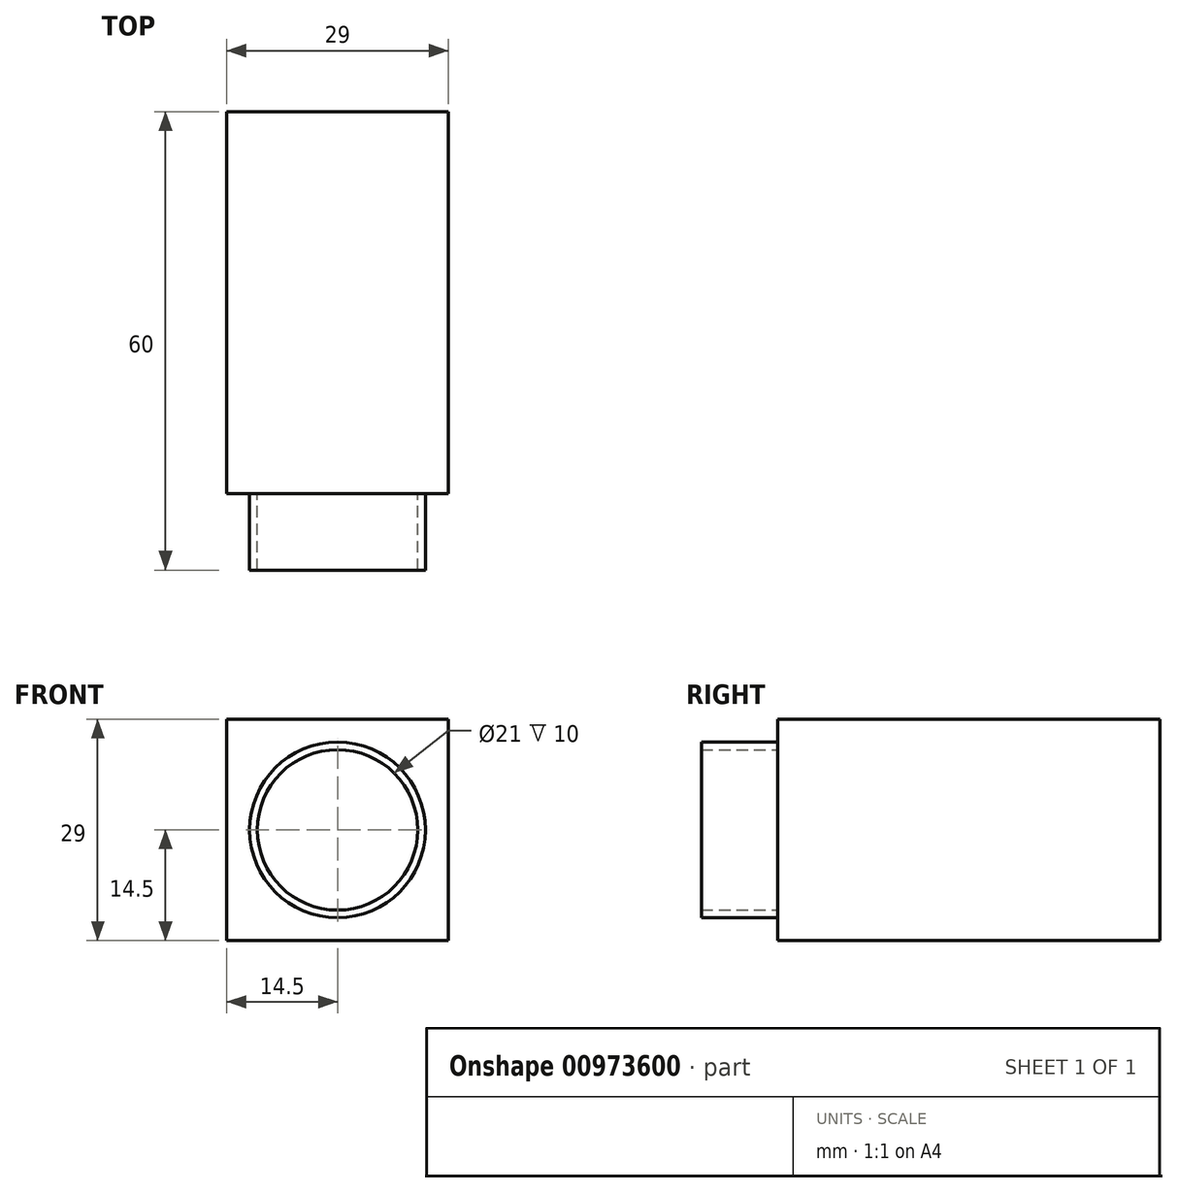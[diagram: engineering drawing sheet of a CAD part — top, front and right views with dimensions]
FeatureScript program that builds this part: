
annotation { "Feature Type Name" : "Feature", "Feature Type Description" : "" }
export const myFeature = defineFeature(function(context is Context, id is Id, definition is map)
    precondition{}
    {
        {
            var Q0;
            Q0=qCreatedBy(makeId("Front.planeOp"),FACE);
            var sketch = newSketch(context, id + "F0", { "sketchPlane" : qUnion([Q0])});
            skLineSegment(sketch, "E0.bottom", {"start": v(14.5, 14.5) * mm, "end": v(-14.5, 14.5) * mm});
            skLineSegment(sketch, "E0.top", {"start": v(14.5, -14.5) * mm, "end": v(-14.5, -14.5) * mm});
            skLineSegment(sketch, "E0.left", {"start": v(14.5, 14.5) * mm, "end": v(14.5, -14.5) * mm});
            skLineSegment(sketch, "E0.right", {"start": v(-14.5, 14.5) * mm, "end": v(-14.5, -14.5) * mm});
            skPoint(sketch, "E0.middle", {"position": v(0, 0) * mm});
            skSolve(sketch);
        }
        {
            var Q0;
            Q0=qSketchRegion(id+"F0",true);
            extrude(context, id + "F1", {"entities" : qUnion([Q0]), "depth" : 50 * mm, "offsetDistance" : 25 * mm});
        }
        {
            var Q0;
            Q0=makeQuery(id+"F1.opExtrude","CAP_FACE",FACE,{"disambiguationData":[OSD([sQuery(id+"F0.wireOp",EDGE,"E0.bottom"),sQuery(id+"F0.wireOp",EDGE,"E0.top"),sQuery(id+"F0.wireOp",EDGE,"E0.left"),sQuery(id+"F0.wireOp",EDGE,"E0.right")])],"isStart":false});
            var sketch = newSketch(context, id + "F2", { "sketchPlane" : qUnion([Q0])});
            skCircle(sketch, "E1", {"center": v(0, 0) * mm, "radius": 11.5 * mm});
            skCircle(sketch, "E2", {"center": v(0, 0) * mm, "radius": 10.5 * mm});
            skSolve(sketch);
        }
        {
            var Q0;
            Q0=qSketchRegion(id+"F2",true);
            extrude(context, id + "F3", {"entities" : qUnion([Q0]), "operationType" : NewBodyOperationType.ADD, "depth" : 10 * mm, "offsetDistance" : 25 * mm});
        }
    });
